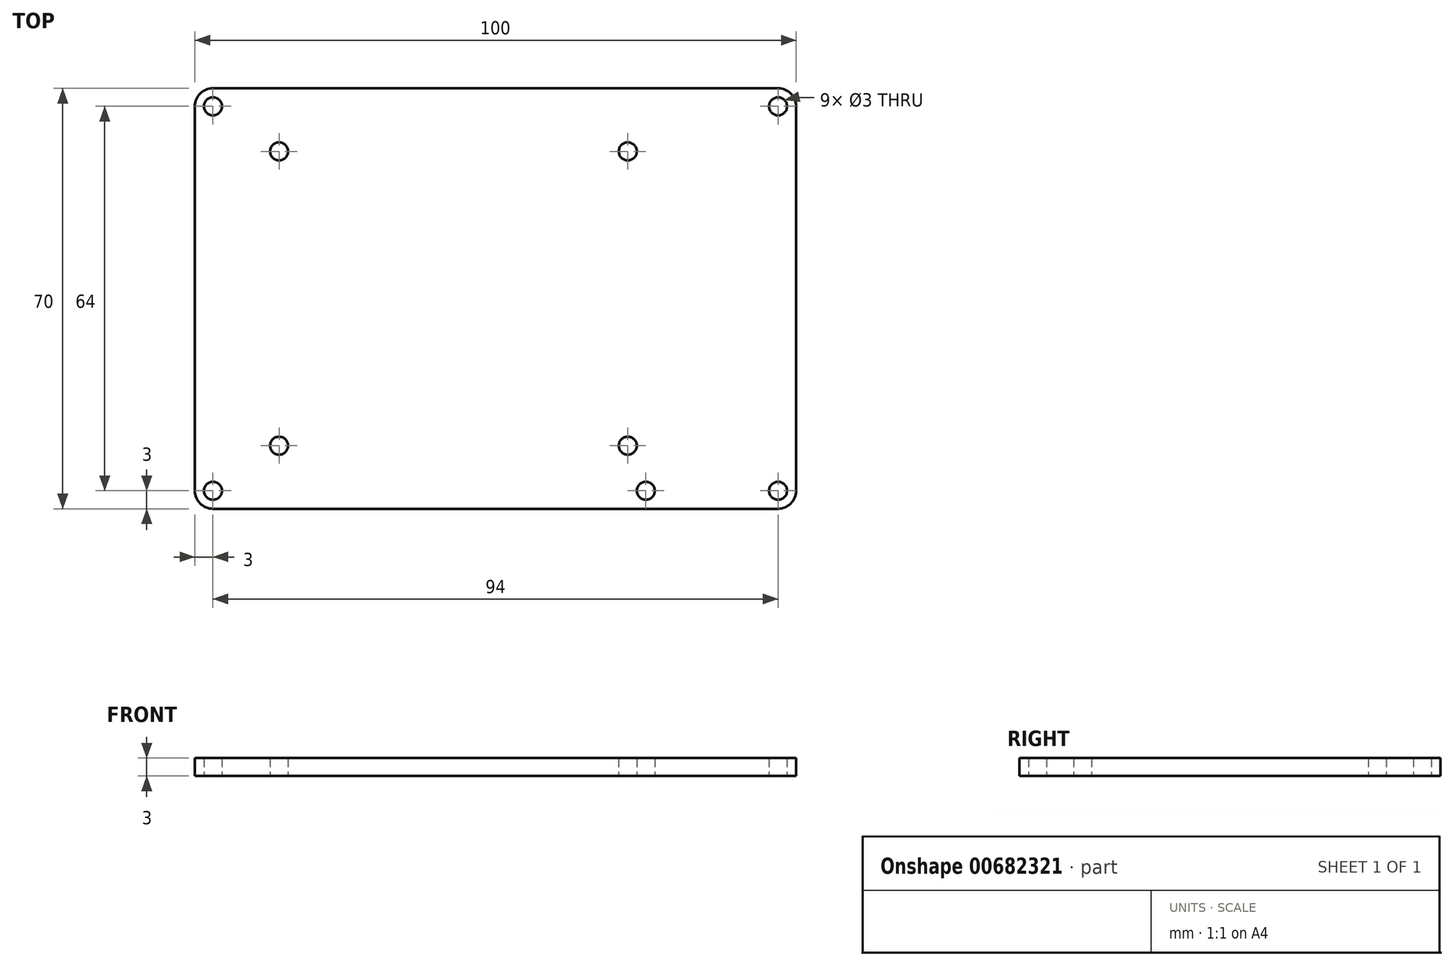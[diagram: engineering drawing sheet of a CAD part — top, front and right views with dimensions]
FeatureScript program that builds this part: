
annotation { "Feature Type Name" : "Feature", "Feature Type Description" : "" }
export const myFeature = defineFeature(function(context is Context, id is Id, definition is map)
    precondition{}
    {
        {
            var Q0;
            Q0=qCreatedBy(makeId("Top.planeOp"),FACE);
            var sketch = newSketch(context, id + "F0", { "sketchPlane" : qUnion([Q0])});
            skLineSegment(sketch, "E0.bottom", {"start": v(3, 0) * mm, "end": v(97, 0) * mm});
            skLineSegment(sketch, "E0.top", {"start": v(3, 70) * mm, "end": v(97, 70) * mm});
            skLineSegment(sketch, "E0.left", {"start": v(0, 3) * mm, "end": v(0, 67) * mm});
            skLineSegment(sketch, "E0.right", {"start": v(100, 3) * mm, "end": v(100, 67) * mm});
            skPoint(sketch, "E1.visualSharp", {"position": v(0, 70) * mm});
            skArc(sketch, "E1.filletArc", {"start": v(3, 70) * mm, "mid": v(0.88, 69.12) * mm, "end": v(0, 67) * mm});
            skPoint(sketch, "E2.visualSharp", {"position": v(100, 70) * mm});
            skArc(sketch, "E2.filletArc", {"start": v(100, 67) * mm, "mid": v(99.12, 69.12) * mm, "end": v(97, 70) * mm});
            skPoint(sketch, "E3.visualSharp", {"position": v(100, 0) * mm});
            skArc(sketch, "E3.filletArc", {"start": v(97, 0) * mm, "mid": v(99.12, 0.88) * mm, "end": v(100, 3) * mm});
            skPoint(sketch, "E4.visualSharp", {"position": v(0, 0) * mm});
            skArc(sketch, "E4.filletArc", {"start": v(0, 3) * mm, "mid": v(0.88, 0.88) * mm, "end": v(3, 0) * mm});
            skCircle(sketch, "E5", {"center": v(3, 67) * mm, "radius": 1.5 * mm});
            skCircle(sketch, "E6", {"center": v(97, 67) * mm, "radius": 1.5 * mm});
            skCircle(sketch, "E7", {"center": v(97, 3) * mm, "radius": 1.5 * mm});
            skCircle(sketch, "E8", {"center": v(3, 3) * mm, "radius": 1.5 * mm});
            skCircle(sketch, "E9", {"center": v(75, 3) * mm, "radius": 1.5 * mm});
            skLineSegment(sketch, "E10", {"start": v(14, 70) * mm, "end": v(14, 0) * mm, "construction": true});
            skLineSegment(sketch, "E11", {"start": v(0, 59.5) * mm, "end": v(100, 59.5) * mm, "construction": true});
            skLineSegment(sketch, "E12", {"start": v(100, 10.5) * mm, "end": v(0, 10.5) * mm, "construction": true});
            skLineSegment(sketch, "E13", {"start": v(72, 0) * mm, "end": v(72, 70) * mm, "construction": true});
            skCircle(sketch, "E14", {"center": v(14, 59.5) * mm, "radius": 1.5 * mm});
            skCircle(sketch, "E15", {"center": v(72, 59.5) * mm, "radius": 1.5 * mm});
            skCircle(sketch, "E16", {"center": v(72, 10.5) * mm, "radius": 1.5 * mm});
            skCircle(sketch, "E17", {"center": v(14, 10.5) * mm, "radius": 1.5 * mm});
            skPoint(sketch, "E18", {"position": v(14, 35) * mm});
            skSolve(sketch);
        }
        {
            var Q0;
            Q0=makeQuery(id+"F0.imprint","IMPRINT",FACE,{"disambiguationData":[TD([[makeQuery(id+"F0.imprint","IMPRINT",EDGE,{"derivedFrom":sQuery(id+"F0.wireOp",EDGE,"E0.bottom")}),1.0]])]});
            extrude(context, id + "F1", {"entities" : qUnion([Q0]), "depth" : 3 * mm, "offsetDistance" : 25 * mm});
        }
    });
